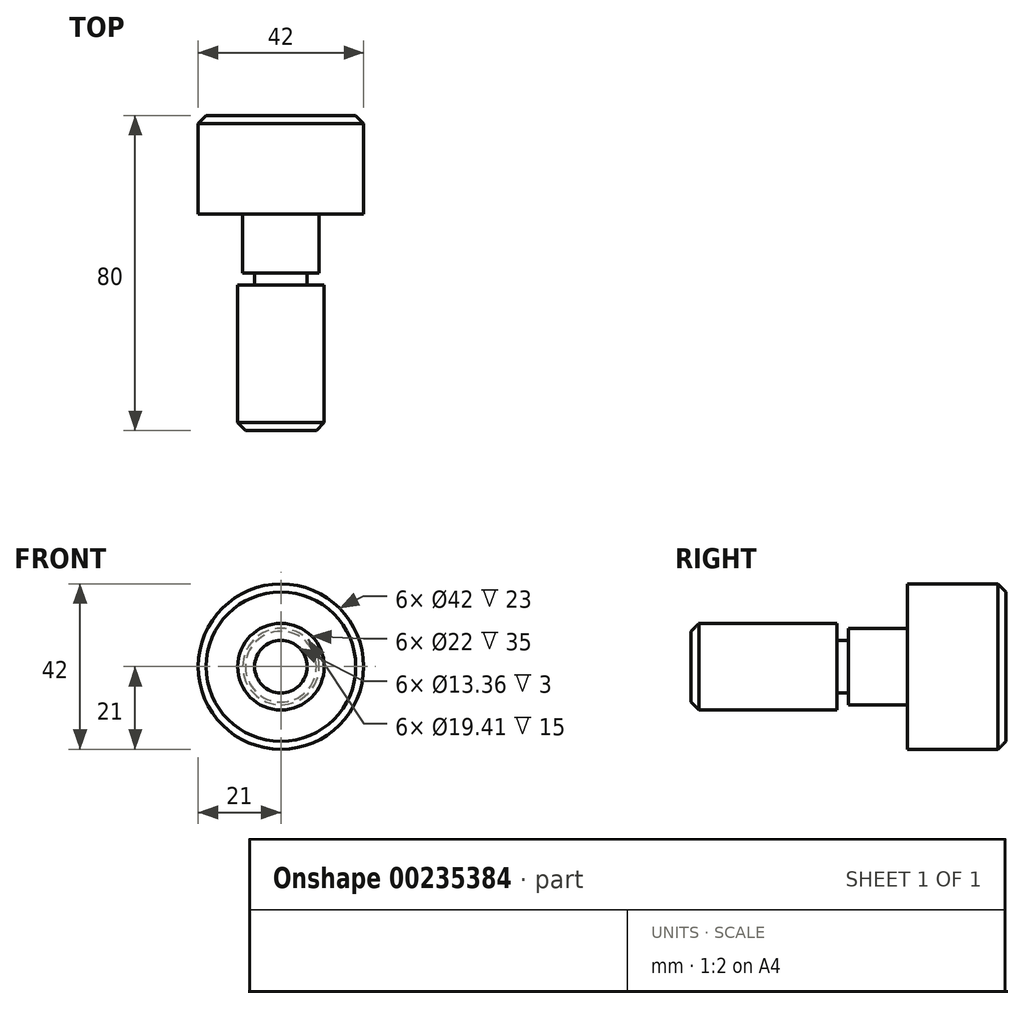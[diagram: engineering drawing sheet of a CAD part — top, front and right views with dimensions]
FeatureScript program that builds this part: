
annotation { "Feature Type Name" : "Feature", "Feature Type Description" : "" }
export const myFeature = defineFeature(function(context is Context, id is Id, definition is map)
    precondition{}
    {
        {
            var Q0;
            Q0=qCreatedBy(makeId("Top.planeOp"),FACE);
            var sketch = newSketch(context, id + "F0", { "sketchPlane" : qUnion([Q0])});
            skLineSegment(sketch, "E0", {"start": v(0, 59.1) * mm, "end": v(0, -63.4) * mm, "construction": true});
            skLineSegment(sketch, "E1", {"start": v(0, 45.56) * mm, "end": v(21, 45.56) * mm});
            skLineSegment(sketch, "E2", {"start": v(21, 45.56) * mm, "end": v(21, 20.56) * mm});
            skLineSegment(sketch, "E3", {"start": v(21, 20.56) * mm, "end": v(9.7, 20.56) * mm});
            skLineSegment(sketch, "E4", {"start": v(9.7, 20.56) * mm, "end": v(9.7, 5.56) * mm});
            skLineSegment(sketch, "E5", {"start": v(9.7, 5.56) * mm, "end": v(6.68, 5.56) * mm});
            skLineSegment(sketch, "E6", {"start": v(6.68, 5.56) * mm, "end": v(6.68, 2.56) * mm});
            skLineSegment(sketch, "E7", {"start": v(6.68, 2.56) * mm, "end": v(11, 2.56) * mm});
            skLineSegment(sketch, "E8", {"start": v(11, 2.56) * mm, "end": v(11, -34.44) * mm});
            skLineSegment(sketch, "E9", {"start": v(11, -34.44) * mm, "end": v(0, -34.44) * mm});
            skSolve(sketch);
        }
        {
            var Q0;
            Q0=sQuery(id+"F0.wireOp",EDGE,"E8");
            var Q1;
            Q1=sQuery(id+"F0.wireOp",EDGE,"E4");
            var Q2;
            Q2=sQuery(id+"F0.wireOp",EDGE,"E9");
            var Q3;
            Q3=sQuery(id+"F0.wireOp",EDGE,"E3");
            var Q4;
            Q4=sQuery(id+"F0.wireOp",EDGE,"E2");
            var Q5;
            Q5=sQuery(id+"F0.wireOp",EDGE,"E1");
            var Q6;
            Q6=sQuery(id+"F0.wireOp",EDGE,"E7");
            var Q7;
            Q7=sQuery(id+"F0.wireOp",EDGE,"E6");
            var Q8;
            Q8=sQuery(id+"F0.wireOp",EDGE,"E5");
            var Q9;
            Q9=sQuery(id+"F0.wireOp",EDGE,"E0");
            revolve(context, id + "F1", {"bodyType" : ToolBodyType.SURFACE, "surfaceEntities" : qUnion([Q0, Q1, Q2, Q3, Q4, Q5, Q6, Q7, Q8]), "axis" : qUnion([Q9]), "revolveType" : RevolveType.FULL});
        }
        {
            var Q0;
            Q0=makeQuery(id+"F1.opRevolve","SWEPT_EDGE",EDGE,{"disambiguationData":[OSD([sQuery(id+"F0.wireOp",VERTEX,"E1.end")])]});
            chamfer(context, id + "F2", {"entities" : qUnion([Q0]), "width" : 2 * mm, "tangentPropagation" : true});
        }
        {
            var Q0;
            Q0=makeQuery(id+"F1.opRevolve","SWEPT_EDGE",EDGE,{"disambiguationData":[OSD([sQuery(id+"F0.wireOp",VERTEX,"E9.start")])]});
            chamfer(context, id + "F3", {"entities" : qUnion([Q0]), "width" : 2 * mm, "tangentPropagation" : true});
        }
    });
